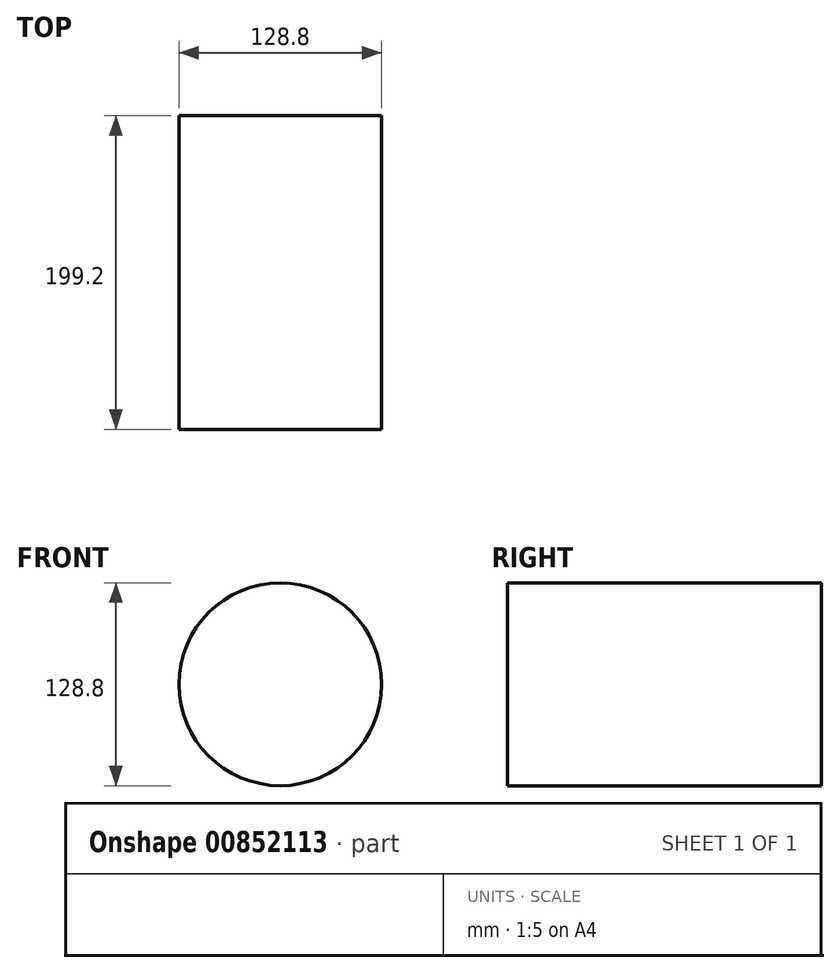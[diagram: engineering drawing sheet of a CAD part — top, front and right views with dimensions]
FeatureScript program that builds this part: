
annotation { "Feature Type Name" : "Feature", "Feature Type Description" : "" }
export const myFeature = defineFeature(function(context is Context, id is Id, definition is map)
    precondition{}
    {
        {
            var Q0;
            Q0=qCreatedBy(makeId("Front.planeOp"),FACE);
            var sketch = newSketch(context, id + "F0", { "sketchPlane" : qUnion([Q0])});
            skCircle(sketch, "E0", {"center": v(0, 0) * mm, "radius": 64.4 * mm});
            skSolve(sketch);
        }
        {
            var Q0;
            Q0 = qSketchRegion(id + "F0", true);
            extrude(context, id + "F1", {"entities" : qUnion([Q0]), "depth" : 199.2 * mm, "offsetDistance" : 25.4 * mm});
        }
    });
